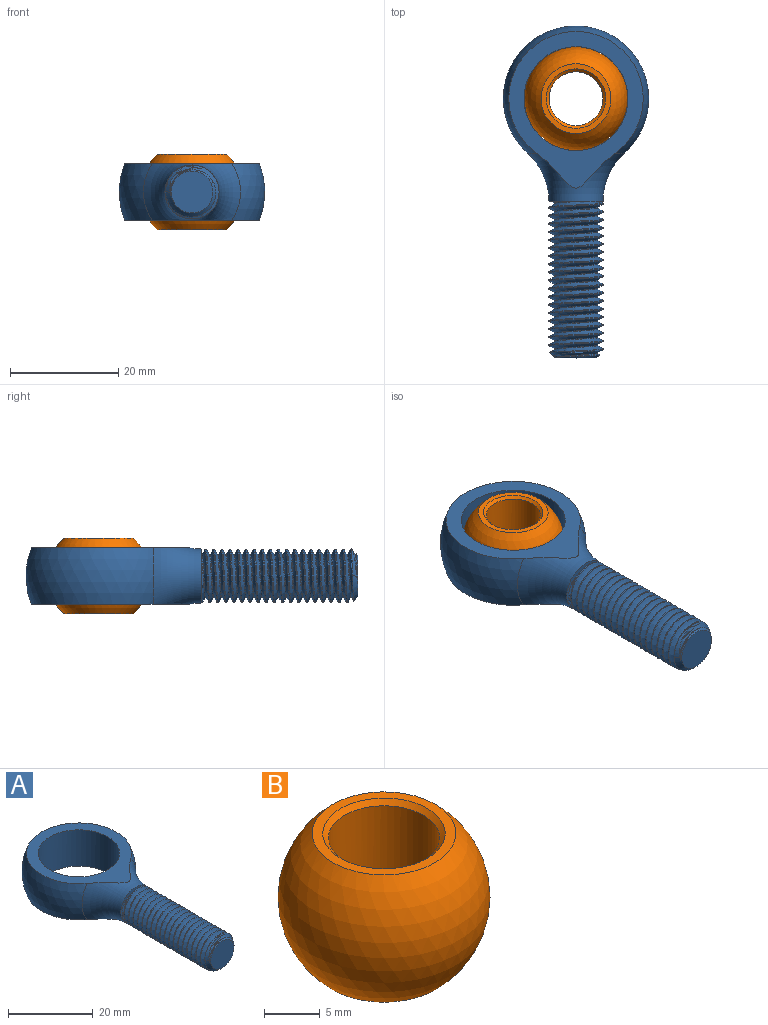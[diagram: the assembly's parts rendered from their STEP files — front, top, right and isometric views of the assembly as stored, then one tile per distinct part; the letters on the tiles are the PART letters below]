
ASSEMBLY  parts=2 mates=1
PART A: 13 faces, bbox 37.4x62.5x37.4 mm
  f0: cylinder r=9.62mm len=19.24mm, axis (0,0,1), area 634.7mm2, adj f11,f12
  f1: sphere r=13.5mm, area 712.6mm2, adj f2,f11,f12
  f2: torus R=16.99mm, axis (0,-1,0), area 269mm2, adj f1,f3,f10,f11,f12
  f3: cylinder r=5mm len=27.88mm, axis (0,1,0), area 109.5mm2, adj f2,f5,f7,f9
  f4: cone r=5mm half-angle=45deg, axis (0,1,0), area 20mm2, adj f5,f6,f7,f8,f9
  f5: cone r=5mm half-angle=45deg, axis (0,1,0), area 4.3mm2, adj f3,f4,f7,f9
  f6: plane 7.75x7.75mm, normal (0,-1,0), area 47.2mm2, adj f4
  f7: bspline ~29.97x9.58mm, area 603.4mm2, adj f3,f4,f5,f8,f10
  f8: bspline ~29.44x8.05mm, area 91.2mm2, adj f4,f7,f9,f10
  f9: bspline ~29.41x10mm, area 603.5mm2, adj f3,f4,f5,f8,f10
  f10: plane 10.61x10.43mm, normal (0,-1,0), area 14.2mm2, adj f2,f7,f8,f9
  f11: plane 29.02x24.88mm, normal (0,0,1), area 220.4mm2, adj f0,f1,f2
  f12: plane 29.02x24.88mm, normal (0,0,-1), area 220.4mm2, adj f0,f1,f2
PART B: 6 faces, bbox 19.1x19.1x14 mm
  f0: cone r=5mm half-angle=45deg, axis (0,0,1), area 23.3mm2, adj f2,f4
  f1: cone r=5.5mm half-angle=45deg, axis (0,0,-1), area 23.3mm2, adj f2,f5
  f2: cylinder r=5mm len=13mm, axis (0,0,1), area 408.4mm2, adj f0,f1
  f3: sphere r=9.53mm, area 837.9mm2, adj f4,f5
  f4: plane 12.92x12.92mm, normal (0,0,1), area 36.1mm2, adj f0,f3
  f5: plane 12.92x12.92mm, normal (0,0,-1), area 36.1mm2, adj f1,f3
PLACE A t=(7.63,-3.92,-9.88)mm
PLACE B t=(7.63,-3.92,-9.88)mm
MATE ball B.f0 <-> A.f0  axis (0,0,1) through (7.63,15.08,-9.88)mm
